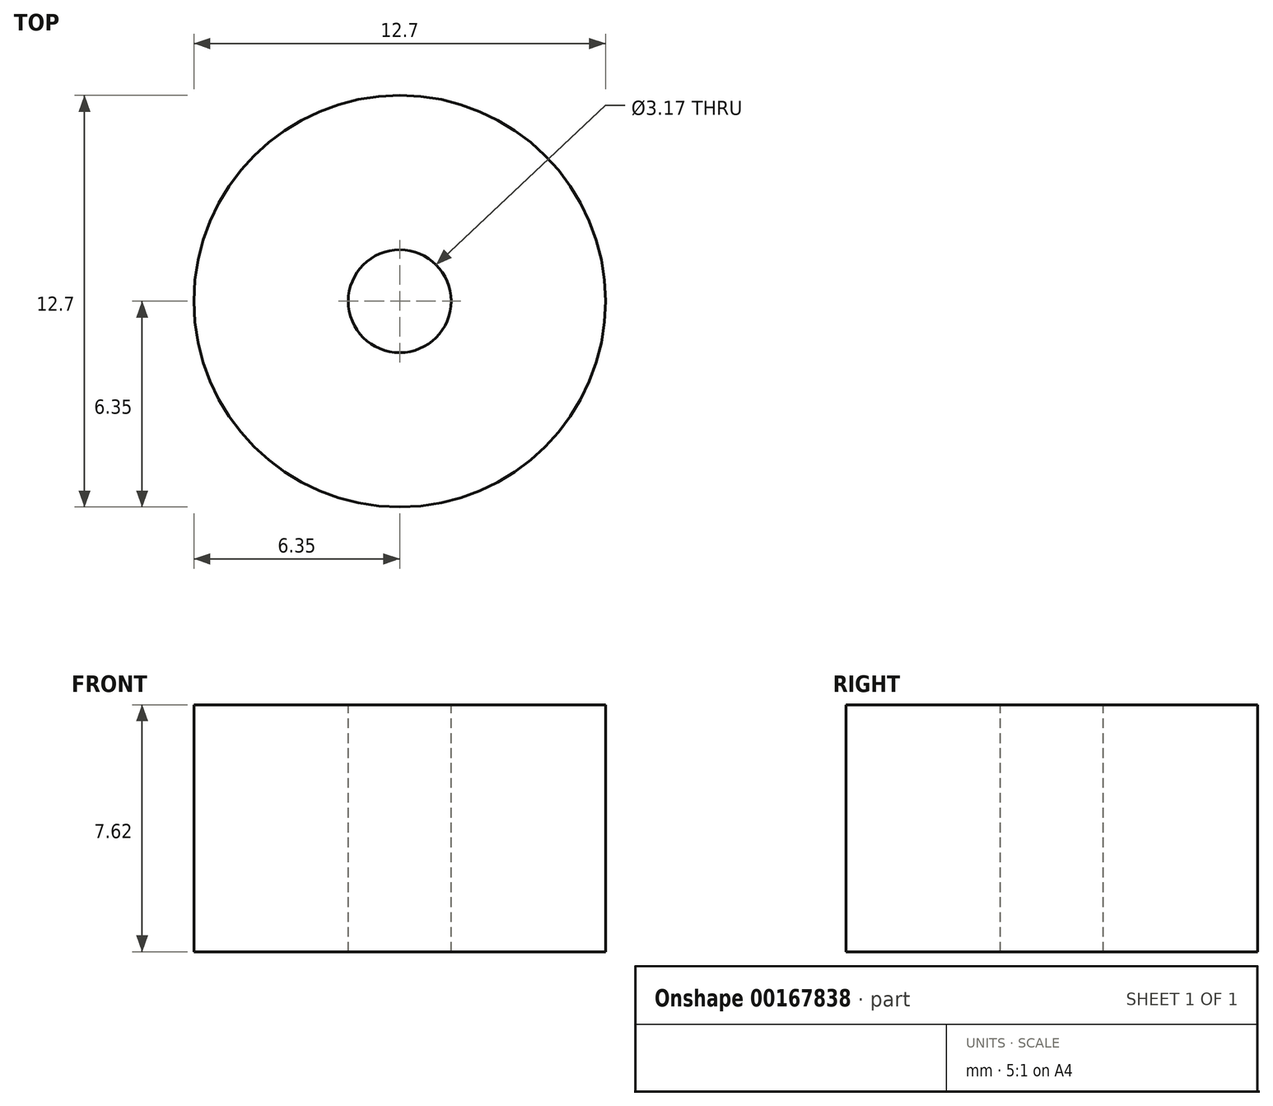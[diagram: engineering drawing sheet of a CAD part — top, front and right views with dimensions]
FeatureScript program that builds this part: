
annotation { "Feature Type Name" : "Feature", "Feature Type Description" : "" }
export const myFeature = defineFeature(function(context is Context, id is Id, definition is map)
    precondition{}
    {
        {
            var Q0;
            Q0=qCreatedBy(makeId("Top.planeOp"),FACE);
            var sketch = newSketch(context, id + "F0", { "sketchPlane" : qUnion([Q0])});
            skCircle(sketch, "E0", {"center": v(0, 0) * mm, "radius": 6.35 * mm});
            skSolve(sketch);
        }
        {
            var Q0;
            Q0 = qSketchRegion(id + "F0", true);
            extrude(context, id + "F1", {"entities" : qUnion([Q0]), "depth" : 7.62 * mm});
        }
        {
            var Q0;
            Q0=makeQuery(id+"F1.opExtrude","CAP_FACE",FACE,{"disambiguationData":[OSD([sQuery(id+"F0.wireOp",EDGE,"E0"),sQuery(id+"F0.wireOp",EDGE,"bRfeOSAl-RVvX-CPhy-aJGS-V5qs9okj35Yr"),sQuery(id+"F0.wireOp",EDGE,"FaJk8tvE-0lQE-VcpX-XuiN-mjfDGw1Wyw8d"),sQuery(id+"F0.wireOp",EDGE,"03f6bd18-6b15-483a-a67a-69e24d5dc7a40.MirrorCS"),sQuery(id+"F0.wireOp",EDGE,"a65229dd-7201-4c94-8c68-d9e8275c4c8f0.MirrorCS"),sQuery(id+"F0.wireOp",EDGE,"bZqA836l-dVkI-6fSC-bMQK-rB0MDRwShzAv"),sQuery(id+"F0.wireOp",EDGE,"1c527023-75f0-4710-8270-c60ef8be72c1.1.0"),sQuery(id+"F0.wireOp",EDGE,"1c527023-75f0-4710-8270-c60ef8be72c1.1.1"),sQuery(id+"F0.wireOp",EDGE,"1c527023-75f0-4710-8270-c60ef8be72c1.1.2"),sQuery(id+"F0.wireOp",EDGE,"1c527023-75f0-4710-8270-c60ef8be72c1.1.3"),sQuery(id+"F0.wireOp",EDGE,"1c527023-75f0-4710-8270-c60ef8be72c1.1.4"),sQuery(id+"F0.wireOp",EDGE,"1c527023-75f0-4710-8270-c60ef8be72c1.2.0"),sQuery(id+"F0.wireOp",EDGE,"1c527023-75f0-4710-8270-c60ef8be72c1.2.1"),sQuery(id+"F0.wireOp",EDGE,"1c527023-75f0-4710-8270-c60ef8be72c1.2.2"),sQuery(id+"F0.wireOp",EDGE,"1c527023-75f0-4710-8270-c60ef8be72c1.2.3"),sQuery(id+"F0.wireOp",EDGE,"1c527023-75f0-4710-8270-c60ef8be72c1.2.4"),sQuery(id+"F0.wireOp",EDGE,"1c527023-75f0-4710-8270-c60ef8be72c1.3.0"),sQuery(id+"F0.wireOp",EDGE,"1c527023-75f0-4710-8270-c60ef8be72c1.3.1"),sQuery(id+"F0.wireOp",EDGE,"1c527023-75f0-4710-8270-c60ef8be72c1.3.2"),sQuery(id+"F0.wireOp",EDGE,"1c527023-75f0-4710-8270-c60ef8be72c1.3.3"),sQuery(id+"F0.wireOp",EDGE,"1c527023-75f0-4710-8270-c60ef8be72c1.3.4"),sQuery(id+"F0.wireOp",EDGE,"1c527023-75f0-4710-8270-c60ef8be72c1.4.0"),sQuery(id+"F0.wireOp",EDGE,"1c527023-75f0-4710-8270-c60ef8be72c1.4.1"),sQuery(id+"F0.wireOp",EDGE,"1c527023-75f0-4710-8270-c60ef8be72c1.4.2"),sQuery(id+"F0.wireOp",EDGE,"1c527023-75f0-4710-8270-c60ef8be72c1.4.3"),sQuery(id+"F0.wireOp",EDGE,"1c527023-75f0-4710-8270-c60ef8be72c1.4.4"),sQuery(id+"F0.wireOp",EDGE,"1c527023-75f0-4710-8270-c60ef8be72c1.5.0"),sQuery(id+"F0.wireOp",EDGE,"1c527023-75f0-4710-8270-c60ef8be72c1.5.1"),sQuery(id+"F0.wireOp",EDGE,"1c527023-75f0-4710-8270-c60ef8be72c1.5.2"),sQuery(id+"F0.wireOp",EDGE,"1c527023-75f0-4710-8270-c60ef8be72c1.5.3"),sQuery(id+"F0.wireOp",EDGE,"1c527023-75f0-4710-8270-c60ef8be72c1.5.4"),sQuery(id+"F0.wireOp",EDGE,"1c527023-75f0-4710-8270-c60ef8be72c1.6.0"),sQuery(id+"F0.wireOp",EDGE,"1c527023-75f0-4710-8270-c60ef8be72c1.6.1"),sQuery(id+"F0.wireOp",EDGE,"1c527023-75f0-4710-8270-c60ef8be72c1.6.2"),sQuery(id+"F0.wireOp",EDGE,"1c527023-75f0-4710-8270-c60ef8be72c1.6.3"),sQuery(id+"F0.wireOp",EDGE,"1c527023-75f0-4710-8270-c60ef8be72c1.6.4"),sQuery(id+"F0.wireOp",EDGE,"1c527023-75f0-4710-8270-c60ef8be72c1.7.0"),sQuery(id+"F0.wireOp",EDGE,"1c527023-75f0-4710-8270-c60ef8be72c1.7.1"),sQuery(id+"F0.wireOp",EDGE,"1c527023-75f0-4710-8270-c60ef8be72c1.7.2"),sQuery(id+"F0.wireOp",EDGE,"1c527023-75f0-4710-8270-c60ef8be72c1.7.3"),sQuery(id+"F0.wireOp",EDGE,"1c527023-75f0-4710-8270-c60ef8be72c1.7.4"),sQuery(id+"F0.wireOp",EDGE,"1c527023-75f0-4710-8270-c60ef8be72c1.8.0"),sQuery(id+"F0.wireOp",EDGE,"1c527023-75f0-4710-8270-c60ef8be72c1.8.1"),sQuery(id+"F0.wireOp",EDGE,"1c527023-75f0-4710-8270-c60ef8be72c1.8.2"),sQuery(id+"F0.wireOp",EDGE,"1c527023-75f0-4710-8270-c60ef8be72c1.8.3"),sQuery(id+"F0.wireOp",EDGE,"1c527023-75f0-4710-8270-c60ef8be72c1.8.4"),sQuery(id+"F0.wireOp",EDGE,"1c527023-75f0-4710-8270-c60ef8be72c1.9.0"),sQuery(id+"F0.wireOp",EDGE,"1c527023-75f0-4710-8270-c60ef8be72c1.9.1"),sQuery(id+"F0.wireOp",EDGE,"1c527023-75f0-4710-8270-c60ef8be72c1.9.2"),sQuery(id+"F0.wireOp",EDGE,"1c527023-75f0-4710-8270-c60ef8be72c1.9.3"),sQuery(id+"F0.wireOp",EDGE,"1c527023-75f0-4710-8270-c60ef8be72c1.9.4"),sQuery(id+"F0.wireOp",EDGE,"1c527023-75f0-4710-8270-c60ef8be72c1.10.0"),sQuery(id+"F0.wireOp",EDGE,"1c527023-75f0-4710-8270-c60ef8be72c1.10.1"),sQuery(id+"F0.wireOp",EDGE,"1c527023-75f0-4710-8270-c60ef8be72c1.10.2"),sQuery(id+"F0.wireOp",EDGE,"1c527023-75f0-4710-8270-c60ef8be72c1.10.3"),sQuery(id+"F0.wireOp",EDGE,"1c527023-75f0-4710-8270-c60ef8be72c1.10.4"),sQuery(id+"F0.wireOp",EDGE,"1c527023-75f0-4710-8270-c60ef8be72c1.11.0"),sQuery(id+"F0.wireOp",EDGE,"1c527023-75f0-4710-8270-c60ef8be72c1.11.1"),sQuery(id+"F0.wireOp",EDGE,"1c527023-75f0-4710-8270-c60ef8be72c1.11.2"),sQuery(id+"F0.wireOp",EDGE,"1c527023-75f0-4710-8270-c60ef8be72c1.11.3"),sQuery(id+"F0.wireOp",EDGE,"1c527023-75f0-4710-8270-c60ef8be72c1.11.4"),sQuery(id+"F0.wireOp",EDGE,"1c527023-75f0-4710-8270-c60ef8be72c1.12.0"),sQuery(id+"F0.wireOp",EDGE,"1c527023-75f0-4710-8270-c60ef8be72c1.12.1"),sQuery(id+"F0.wireOp",EDGE,"1c527023-75f0-4710-8270-c60ef8be72c1.12.2"),sQuery(id+"F0.wireOp",EDGE,"1c527023-75f0-4710-8270-c60ef8be72c1.12.3"),sQuery(id+"F0.wireOp",EDGE,"1c527023-75f0-4710-8270-c60ef8be72c1.12.4"),sQuery(id+"F0.wireOp",EDGE,"1c527023-75f0-4710-8270-c60ef8be72c1.13.0"),sQuery(id+"F0.wireOp",EDGE,"1c527023-75f0-4710-8270-c60ef8be72c1.13.1"),sQuery(id+"F0.wireOp",EDGE,"1c527023-75f0-4710-8270-c60ef8be72c1.13.2"),sQuery(id+"F0.wireOp",EDGE,"1c527023-75f0-4710-8270-c60ef8be72c1.13.3"),sQuery(id+"F0.wireOp",EDGE,"1c527023-75f0-4710-8270-c60ef8be72c1.13.4"),sQuery(id+"F0.wireOp",EDGE,"1c527023-75f0-4710-8270-c60ef8be72c1.14.0"),sQuery(id+"F0.wireOp",EDGE,"1c527023-75f0-4710-8270-c60ef8be72c1.14.1"),sQuery(id+"F0.wireOp",EDGE,"1c527023-75f0-4710-8270-c60ef8be72c1.14.2"),sQuery(id+"F0.wireOp",EDGE,"1c527023-75f0-4710-8270-c60ef8be72c1.14.3"),sQuery(id+"F0.wireOp",EDGE,"1c527023-75f0-4710-8270-c60ef8be72c1.14.4"),sQuery(id+"F0.wireOp",EDGE,"1c527023-75f0-4710-8270-c60ef8be72c1.15.0"),sQuery(id+"F0.wireOp",EDGE,"1c527023-75f0-4710-8270-c60ef8be72c1.15.1"),sQuery(id+"F0.wireOp",EDGE,"1c527023-75f0-4710-8270-c60ef8be72c1.15.2"),sQuery(id+"F0.wireOp",EDGE,"1c527023-75f0-4710-8270-c60ef8be72c1.15.3"),sQuery(id+"F0.wireOp",EDGE,"1c527023-75f0-4710-8270-c60ef8be72c1.15.4")])],"isStart":false});
            var sketch = newSketch(context, id + "F2", { "sketchPlane" : qUnion([Q0])});
            skCircle(sketch, "E1", {"center": v(0, 0) * mm, "radius": 1.59 * mm});
            skSolve(sketch);
        }
        {
            var Q0;
            Q0 = qSketchRegion(id + "F2", true);
            var Q1;
            Q1=makeQuery(id+"F1.opExtrude","CAP_FACE",FACE,{"disambiguationData":[OSD([sQuery(id+"F0.wireOp",EDGE,"E0"),sQuery(id+"F0.wireOp",EDGE,"bRfeOSAl-RVvX-CPhy-aJGS-V5qs9okj35Yr"),sQuery(id+"F0.wireOp",EDGE,"FaJk8tvE-0lQE-VcpX-XuiN-mjfDGw1Wyw8d"),sQuery(id+"F0.wireOp",EDGE,"03f6bd18-6b15-483a-a67a-69e24d5dc7a40.MirrorCS"),sQuery(id+"F0.wireOp",EDGE,"a65229dd-7201-4c94-8c68-d9e8275c4c8f0.MirrorCS"),sQuery(id+"F0.wireOp",EDGE,"bZqA836l-dVkI-6fSC-bMQK-rB0MDRwShzAv"),sQuery(id+"F0.wireOp",EDGE,"1c527023-75f0-4710-8270-c60ef8be72c1.1.0"),sQuery(id+"F0.wireOp",EDGE,"1c527023-75f0-4710-8270-c60ef8be72c1.1.1"),sQuery(id+"F0.wireOp",EDGE,"1c527023-75f0-4710-8270-c60ef8be72c1.1.2"),sQuery(id+"F0.wireOp",EDGE,"1c527023-75f0-4710-8270-c60ef8be72c1.1.3"),sQuery(id+"F0.wireOp",EDGE,"1c527023-75f0-4710-8270-c60ef8be72c1.1.4"),sQuery(id+"F0.wireOp",EDGE,"1c527023-75f0-4710-8270-c60ef8be72c1.2.0"),sQuery(id+"F0.wireOp",EDGE,"1c527023-75f0-4710-8270-c60ef8be72c1.2.1"),sQuery(id+"F0.wireOp",EDGE,"1c527023-75f0-4710-8270-c60ef8be72c1.2.2"),sQuery(id+"F0.wireOp",EDGE,"1c527023-75f0-4710-8270-c60ef8be72c1.2.3"),sQuery(id+"F0.wireOp",EDGE,"1c527023-75f0-4710-8270-c60ef8be72c1.2.4"),sQuery(id+"F0.wireOp",EDGE,"1c527023-75f0-4710-8270-c60ef8be72c1.3.0"),sQuery(id+"F0.wireOp",EDGE,"1c527023-75f0-4710-8270-c60ef8be72c1.3.1"),sQuery(id+"F0.wireOp",EDGE,"1c527023-75f0-4710-8270-c60ef8be72c1.3.2"),sQuery(id+"F0.wireOp",EDGE,"1c527023-75f0-4710-8270-c60ef8be72c1.3.3"),sQuery(id+"F0.wireOp",EDGE,"1c527023-75f0-4710-8270-c60ef8be72c1.3.4"),sQuery(id+"F0.wireOp",EDGE,"1c527023-75f0-4710-8270-c60ef8be72c1.4.0"),sQuery(id+"F0.wireOp",EDGE,"1c527023-75f0-4710-8270-c60ef8be72c1.4.1"),sQuery(id+"F0.wireOp",EDGE,"1c527023-75f0-4710-8270-c60ef8be72c1.4.2"),sQuery(id+"F0.wireOp",EDGE,"1c527023-75f0-4710-8270-c60ef8be72c1.4.3"),sQuery(id+"F0.wireOp",EDGE,"1c527023-75f0-4710-8270-c60ef8be72c1.4.4"),sQuery(id+"F0.wireOp",EDGE,"1c527023-75f0-4710-8270-c60ef8be72c1.5.0"),sQuery(id+"F0.wireOp",EDGE,"1c527023-75f0-4710-8270-c60ef8be72c1.5.1"),sQuery(id+"F0.wireOp",EDGE,"1c527023-75f0-4710-8270-c60ef8be72c1.5.2"),sQuery(id+"F0.wireOp",EDGE,"1c527023-75f0-4710-8270-c60ef8be72c1.5.3"),sQuery(id+"F0.wireOp",EDGE,"1c527023-75f0-4710-8270-c60ef8be72c1.5.4"),sQuery(id+"F0.wireOp",EDGE,"1c527023-75f0-4710-8270-c60ef8be72c1.6.0"),sQuery(id+"F0.wireOp",EDGE,"1c527023-75f0-4710-8270-c60ef8be72c1.6.1"),sQuery(id+"F0.wireOp",EDGE,"1c527023-75f0-4710-8270-c60ef8be72c1.6.2"),sQuery(id+"F0.wireOp",EDGE,"1c527023-75f0-4710-8270-c60ef8be72c1.6.3"),sQuery(id+"F0.wireOp",EDGE,"1c527023-75f0-4710-8270-c60ef8be72c1.6.4"),sQuery(id+"F0.wireOp",EDGE,"1c527023-75f0-4710-8270-c60ef8be72c1.7.0"),sQuery(id+"F0.wireOp",EDGE,"1c527023-75f0-4710-8270-c60ef8be72c1.7.1"),sQuery(id+"F0.wireOp",EDGE,"1c527023-75f0-4710-8270-c60ef8be72c1.7.2"),sQuery(id+"F0.wireOp",EDGE,"1c527023-75f0-4710-8270-c60ef8be72c1.7.3"),sQuery(id+"F0.wireOp",EDGE,"1c527023-75f0-4710-8270-c60ef8be72c1.7.4"),sQuery(id+"F0.wireOp",EDGE,"1c527023-75f0-4710-8270-c60ef8be72c1.8.0"),sQuery(id+"F0.wireOp",EDGE,"1c527023-75f0-4710-8270-c60ef8be72c1.8.1"),sQuery(id+"F0.wireOp",EDGE,"1c527023-75f0-4710-8270-c60ef8be72c1.8.2"),sQuery(id+"F0.wireOp",EDGE,"1c527023-75f0-4710-8270-c60ef8be72c1.8.3"),sQuery(id+"F0.wireOp",EDGE,"1c527023-75f0-4710-8270-c60ef8be72c1.8.4"),sQuery(id+"F0.wireOp",EDGE,"1c527023-75f0-4710-8270-c60ef8be72c1.9.0"),sQuery(id+"F0.wireOp",EDGE,"1c527023-75f0-4710-8270-c60ef8be72c1.9.1"),sQuery(id+"F0.wireOp",EDGE,"1c527023-75f0-4710-8270-c60ef8be72c1.9.2"),sQuery(id+"F0.wireOp",EDGE,"1c527023-75f0-4710-8270-c60ef8be72c1.9.3"),sQuery(id+"F0.wireOp",EDGE,"1c527023-75f0-4710-8270-c60ef8be72c1.9.4"),sQuery(id+"F0.wireOp",EDGE,"1c527023-75f0-4710-8270-c60ef8be72c1.10.0"),sQuery(id+"F0.wireOp",EDGE,"1c527023-75f0-4710-8270-c60ef8be72c1.10.1"),sQuery(id+"F0.wireOp",EDGE,"1c527023-75f0-4710-8270-c60ef8be72c1.10.2"),sQuery(id+"F0.wireOp",EDGE,"1c527023-75f0-4710-8270-c60ef8be72c1.10.3"),sQuery(id+"F0.wireOp",EDGE,"1c527023-75f0-4710-8270-c60ef8be72c1.10.4"),sQuery(id+"F0.wireOp",EDGE,"1c527023-75f0-4710-8270-c60ef8be72c1.11.0"),sQuery(id+"F0.wireOp",EDGE,"1c527023-75f0-4710-8270-c60ef8be72c1.11.1"),sQuery(id+"F0.wireOp",EDGE,"1c527023-75f0-4710-8270-c60ef8be72c1.11.2"),sQuery(id+"F0.wireOp",EDGE,"1c527023-75f0-4710-8270-c60ef8be72c1.11.3"),sQuery(id+"F0.wireOp",EDGE,"1c527023-75f0-4710-8270-c60ef8be72c1.11.4"),sQuery(id+"F0.wireOp",EDGE,"1c527023-75f0-4710-8270-c60ef8be72c1.12.0"),sQuery(id+"F0.wireOp",EDGE,"1c527023-75f0-4710-8270-c60ef8be72c1.12.1"),sQuery(id+"F0.wireOp",EDGE,"1c527023-75f0-4710-8270-c60ef8be72c1.12.2"),sQuery(id+"F0.wireOp",EDGE,"1c527023-75f0-4710-8270-c60ef8be72c1.12.3"),sQuery(id+"F0.wireOp",EDGE,"1c527023-75f0-4710-8270-c60ef8be72c1.12.4"),sQuery(id+"F0.wireOp",EDGE,"1c527023-75f0-4710-8270-c60ef8be72c1.13.0"),sQuery(id+"F0.wireOp",EDGE,"1c527023-75f0-4710-8270-c60ef8be72c1.13.1"),sQuery(id+"F0.wireOp",EDGE,"1c527023-75f0-4710-8270-c60ef8be72c1.13.2"),sQuery(id+"F0.wireOp",EDGE,"1c527023-75f0-4710-8270-c60ef8be72c1.13.3"),sQuery(id+"F0.wireOp",EDGE,"1c527023-75f0-4710-8270-c60ef8be72c1.13.4"),sQuery(id+"F0.wireOp",EDGE,"1c527023-75f0-4710-8270-c60ef8be72c1.14.0"),sQuery(id+"F0.wireOp",EDGE,"1c527023-75f0-4710-8270-c60ef8be72c1.14.1"),sQuery(id+"F0.wireOp",EDGE,"1c527023-75f0-4710-8270-c60ef8be72c1.14.2"),sQuery(id+"F0.wireOp",EDGE,"1c527023-75f0-4710-8270-c60ef8be72c1.14.3"),sQuery(id+"F0.wireOp",EDGE,"1c527023-75f0-4710-8270-c60ef8be72c1.14.4"),sQuery(id+"F0.wireOp",EDGE,"1c527023-75f0-4710-8270-c60ef8be72c1.15.0"),sQuery(id+"F0.wireOp",EDGE,"1c527023-75f0-4710-8270-c60ef8be72c1.15.1"),sQuery(id+"F0.wireOp",EDGE,"1c527023-75f0-4710-8270-c60ef8be72c1.15.2"),sQuery(id+"F0.wireOp",EDGE,"1c527023-75f0-4710-8270-c60ef8be72c1.15.3"),sQuery(id+"F0.wireOp",EDGE,"1c527023-75f0-4710-8270-c60ef8be72c1.15.4")])],"isStart":true});
            extrude(context, id + "F3", {"entities" : qUnion([Q0]), "operationType" : NewBodyOperationType.REMOVE, "endBound" : BoundingType.UP_TO_SURFACE, "oppositeDirection" : true, "endBoundEntityFace" : qUnion([Q1]), "depth" : 25.4 * mm});
        }
    });
